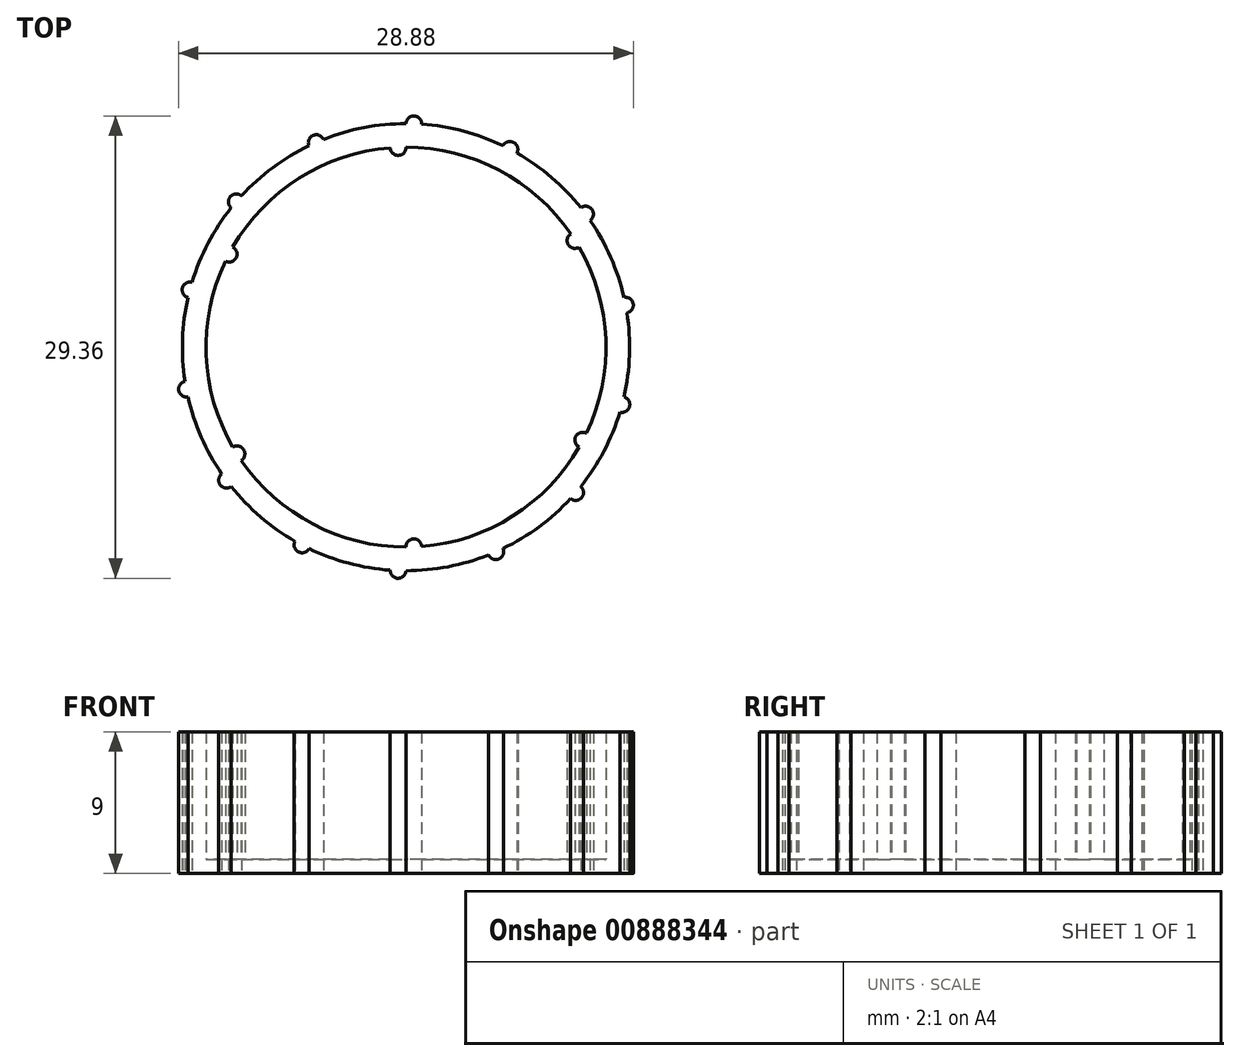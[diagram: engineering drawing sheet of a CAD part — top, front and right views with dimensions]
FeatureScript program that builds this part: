
annotation { "Feature Type Name" : "Feature", "Feature Type Description" : "" }
export const myFeature = defineFeature(function(context is Context, id is Id, definition is map)
    precondition{}
    {
        {
            var Q0;
            Q0=qCreatedBy(makeId("Top.planeOp"),FACE);
            var sketch = newSketch(context, id + "F0", { "sketchPlane" : qUnion([Q0])});
            skArc(sketch, "E0", {"start": v(-1, 12.66) * mm, "mid": v(-6.78, 10.74) * mm, "end": v(-11, 6.35) * mm});
            skArc(sketch, "E1", {"start": v(0, 14.2) * mm, "mid": v(-2.67, 13.95) * mm, "end": v(-5.25, 13.2) * mm});
            skArc(sketch, "E2", {"start": v(-1, 12.66) * mm, "mid": v(-0.48, 12.18) * mm, "end": v(0, 12.7) * mm});
            skArc(sketch, "E3.1.0", {"start": v(-11.46, 5.46) * mm, "mid": v(-10.79, 5.67) * mm, "end": v(-11, 6.35) * mm});
            skArc(sketch, "E3.2.0", {"start": v(-10.46, -7.2) * mm, "mid": v(-10.3, -6.5) * mm, "end": v(-11, -6.35) * mm});
            skArc(sketch, "E4.2.3.0", {"start": v(1, -12.66) * mm, "mid": v(0.48, -12.18) * mm, "end": v(0, -12.7) * mm});
            skArc(sketch, "E4.2.4.0", {"start": v(11.46, -5.46) * mm, "mid": v(10.79, -5.67) * mm, "end": v(11, -6.35) * mm});
            skArc(sketch, "E4.2.5.0", {"start": v(10.46, 7.2) * mm, "mid": v(10.3, 6.5) * mm, "end": v(11, 6.35) * mm});
            skArc(sketch, "E5.trimOffspring", {"start": v(-11.46, 5.46) * mm, "mid": v(-12.7, -0.5) * mm, "end": v(-11, -6.35) * mm});
            skArc(sketch, "E6.trimOffspring", {"start": v(-10.46, -7.2) * mm, "mid": v(-5.91, -11.24) * mm, "end": v(0, -12.7) * mm});
            skArc(sketch, "E7.trimOffspring", {"start": v(1, -12.66) * mm, "mid": v(6.78, -10.74) * mm, "end": v(11, -6.35) * mm});
            skArc(sketch, "E8.trimOffspring", {"start": v(11.46, -5.46) * mm, "mid": v(12.7, 0.5) * mm, "end": v(11, 6.35) * mm});
            skArc(sketch, "E9.trimOffspring", {"start": v(10.46, 7.2) * mm, "mid": v(5.91, 11.24) * mm, "end": v(0, 12.7) * mm});
            skArc(sketch, "E10", {"start": v(1, 14.16) * mm, "mid": v(0.52, 14.68) * mm, "end": v(0, 14.2) * mm});
            skArc(sketch, "E11.1.0", {"start": v(-5.25, 13.2) * mm, "mid": v(-5.9, 13.45) * mm, "end": v(-6.16, 12.8) * mm});
            skArc(sketch, "E11.2.0", {"start": v(-10.45, 9.61) * mm, "mid": v(-11.16, 9.56) * mm, "end": v(-11.1, 8.85) * mm});
            skArc(sketch, "E12.3.3.0", {"start": v(-13.59, 4.13) * mm, "mid": v(-14.2, 3.77) * mm, "end": v(-13.84, 3.16) * mm});
            skArc(sketch, "E12.3.4.0", {"start": v(-14.03, -2.18) * mm, "mid": v(-14.43, -2.76) * mm, "end": v(-13.84, -3.16) * mm});
            skArc(sketch, "E12.3.5.0", {"start": v(-11.7, -8.05) * mm, "mid": v(-11.8, -8.75) * mm, "end": v(-11.1, -8.85) * mm});
            skArc(sketch, "E12.3.6.0", {"start": v(-7.05, -12.33) * mm, "mid": v(-6.84, -13) * mm, "end": v(-6.16, -12.8) * mm});
            skArc(sketch, "E13.3.7.0", {"start": v(-1, -14.16) * mm, "mid": v(-0.52, -14.68) * mm, "end": v(0, -14.2) * mm});
            skArc(sketch, "E13.3.8.0", {"start": v(5.25, -13.2) * mm, "mid": v(5.9, -13.45) * mm, "end": v(6.16, -12.8) * mm});
            skArc(sketch, "E13.3.9.0", {"start": v(10.45, -9.61) * mm, "mid": v(11.16, -9.56) * mm, "end": v(11.1, -8.85) * mm});
            skArc(sketch, "E13.3.10.0", {"start": v(13.59, -4.13) * mm, "mid": v(14.2, -3.77) * mm, "end": v(13.84, -3.16) * mm});
            skArc(sketch, "E13.3.11.0", {"start": v(14.03, 2.18) * mm, "mid": v(14.43, 2.76) * mm, "end": v(13.84, 3.16) * mm});
            skArc(sketch, "E13.3.12.0", {"start": v(11.7, 8.05) * mm, "mid": v(11.8, 8.75) * mm, "end": v(11.1, 8.85) * mm});
            skArc(sketch, "E13.3.13.0", {"start": v(7.05, 12.33) * mm, "mid": v(6.84, 13) * mm, "end": v(6.16, 12.8) * mm});
            skArc(sketch, "E14.trimOffspring", {"start": v(6.16, 12.8) * mm, "mid": v(3.65, 13.72) * mm, "end": v(1, 14.16) * mm});
            skArc(sketch, "E15.trimOffspring", {"start": v(11.1, 8.85) * mm, "mid": v(9.24, 10.78) * mm, "end": v(7.05, 12.33) * mm});
            skArc(sketch, "E16.trimOffspring", {"start": v(13.84, 3.16) * mm, "mid": v(13, 5.7) * mm, "end": v(11.7, 8.05) * mm});
            skArc(sketch, "E17.trimOffspring", {"start": v(13.84, -3.16) * mm, "mid": v(14.2, -0.5) * mm, "end": v(14.03, 2.18) * mm});
            skArc(sketch, "E18.trimOffspring", {"start": v(11.1, -8.85) * mm, "mid": v(12.57, -6.6) * mm, "end": v(13.59, -4.13) * mm});
            skArc(sketch, "E19.trimOffspring", {"start": v(6.16, -12.8) * mm, "mid": v(8.46, -11.4) * mm, "end": v(10.45, -9.61) * mm});
            skArc(sketch, "E20.trimOffspring", {"start": v(0, -14.2) * mm, "mid": v(2.67, -13.95) * mm, "end": v(5.25, -13.2) * mm});
            skArc(sketch, "E21.trimOffspring", {"start": v(-6.16, -12.8) * mm, "mid": v(-3.65, -13.72) * mm, "end": v(-1, -14.16) * mm});
            skArc(sketch, "E22.trimOffspring", {"start": v(-11.1, -8.85) * mm, "mid": v(-9.24, -10.78) * mm, "end": v(-7.05, -12.33) * mm});
            skArc(sketch, "E23.trimOffspring", {"start": v(-13.84, -3.16) * mm, "mid": v(-13, -5.7) * mm, "end": v(-11.7, -8.05) * mm});
            skArc(sketch, "E24.trimOffspring", {"start": v(-13.84, 3.16) * mm, "mid": v(-14.2, 0.5) * mm, "end": v(-14.03, -2.18) * mm});
            skArc(sketch, "E25.trimOffspring", {"start": v(-11.1, 8.85) * mm, "mid": v(-12.57, 6.6) * mm, "end": v(-13.59, 4.13) * mm});
            skArc(sketch, "E26.trimOffspring", {"start": v(-6.16, 12.8) * mm, "mid": v(-8.46, 11.4) * mm, "end": v(-10.45, 9.61) * mm});
            skSolve(sketch);
        }
        {
            var Q0;
            Q0=makeQuery(id+"F0.imprint","IMPRINT",FACE,{"disambiguationData":[TD([[makeQuery(id+"F0.imprint","IMPRINT",EDGE,{"derivedFrom":sQuery(id+"F0.wireOp",EDGE,"E0")}),1.0]])]});
            extrude(context, id + "F1", {"entities" : qUnion([Q0]), "depth" : 0.9 * mm, "offsetDistance" : 25 * mm});
        }
        {
            var Q0;
            Q0=makeQuery(id+"F0.imprint","IMPRINT",FACE,{"disambiguationData":[TD([[makeQuery(id+"F0.imprint","IMPRINT",EDGE,{"derivedFrom":sQuery(id+"F0.wireOp",EDGE,"E0")}),-1.0]])]});
            extrude(context, id + "F2", {"entities" : qUnion([Q0]), "operationType" : NewBodyOperationType.ADD, "depth" : 9 * mm, "offsetDistance" : 25 * mm});
        }
    });
